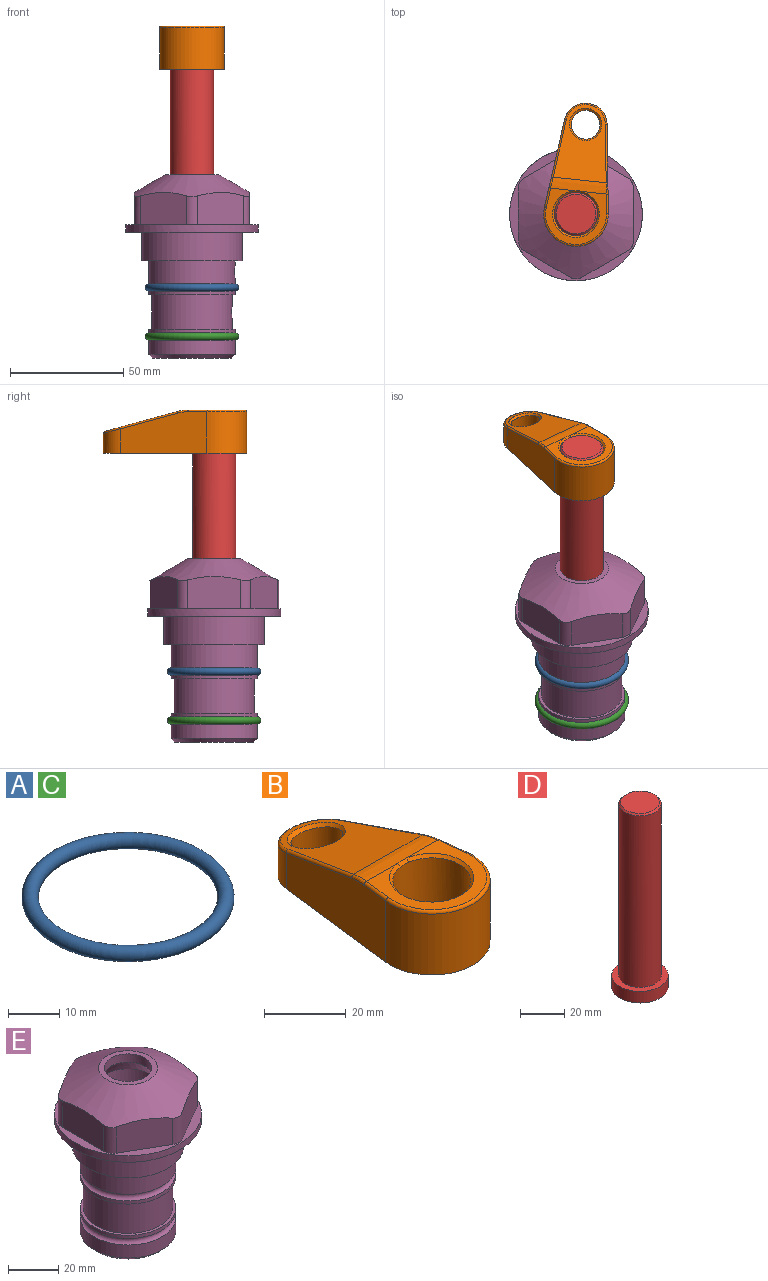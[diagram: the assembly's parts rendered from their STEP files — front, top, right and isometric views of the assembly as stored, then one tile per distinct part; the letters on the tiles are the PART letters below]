
ASSEMBLY  parts=5 mates=4
PART A: 1 faces, bbox 44.7x44.7x3.2 mm
  f0: torus R=19.05mm, axis (0,0,1), area 1193.9mm2
PART B: 31 faces, bbox 31.7x65.5x19.8 mm
  f0: plane 39.12x18.26mm, normal (0.99,0.12,0), area 612.2mm2, adj f1,f4,f7,f11,f13,f15
  f1: cylinder r=9.53mm len=18.91mm, axis (0,0,-1), area 296.1mm2, adj f0,f2,f7,f17
  f2: plane 39.12x18.26mm, normal (-0.99,0.12,0), area 612.2mm2, adj f1,f4,f7,f12,f14,f16
  f3: cylinder r=6.35mm len=12.7mm, axis (0,0,-1), area 362.4mm2, adj f7,f18
  f4: cylinder r=14.29mm len=28.58mm, axis (0,0,-1), area 882.2mm2, adj f0,f2,f7,f10
  f5: cylinder r=9.53mm len=19.05mm, axis (0,0,-1), area 1092.6mm2, adj f7,f19,f20
  f6: plane 26.99x23.69mm, normal (0,0,1), area 216.2mm2, adj f9,f10,f11,f12,f19
  f7: plane 63.5x28.58mm, normal (0,0,-1), area 661.8mm2, adj f0,f1,f2,f3,f4,f5,f22,f23
  f8: plane 33.52x23.6mm, normal (0,0.26,0.97), area 486mm2, adj f9,f15,f16,f17,f18
  f9: cylinder r=19.05mm len=24.72mm, axis (1,0,0), area 120.4mm2, adj f6,f8,f13,f14,f20
  f10: torus R=13.49mm, axis (0,0,1), area 59mm2, adj f4,f6,f11,f12
  f11: cylinder r=0.79mm len=8.67mm, axis (0.12,-0.99,0), area 10.8mm2, adj f0,f6,f10,f13
  f12: cylinder r=0.79mm len=8.67mm, axis (0.12,0.99,0), area 10.8mm2, adj f2,f6,f10,f14
  f13: bspline ~4.95x1.42mm, area 6.1mm2, adj f0,f9,f11,f15
  f14: bspline ~4.95x1.42mm, area 6.1mm2, adj f2,f9,f12,f16
  f15: cylinder r=0.79mm len=25.95mm, axis (0.12,-0.96,0.26), area 32.9mm2, adj f0,f8,f13,f17
  f16: cylinder r=0.79mm len=25.95mm, axis (0.12,0.96,-0.26), area 32.9mm2, adj f2,f8,f14,f17
  f17: bspline ~18.91x8.38mm, area 30mm2, adj f1,f8,f15,f16
  f18: bspline ~14.29x14.29mm, area 48.3mm2, adj f3,f8
  f19: cone r=9.53mm half-angle=45deg, axis (0,0,1), area 66.5mm2, adj f5,f6,f20
  f20: bspline ~3.22x0.96mm, area 3.5mm2, adj f5,f9,f19
  f21: plane 2.75x2.72mm, normal (0,0,-1), area 2.9mm2, adj f23,f25,f28
  f22: plane 23.05x15.88mm, normal (-0.99,-0.12,0), area 323.6mm2, adj f7,f25,f26,f27,f28,f29
  f23: plane 23.05x15.88mm, normal (0.99,-0.12,0), area 323.6mm2, adj f7,f21,f25,f27,f28,f30
  f24: cylinder r=9.53mm len=10.69mm, axis (0,0,-1), area 114.7mm2, adj f7,f27,f29,f30
  f25: cylinder r=12.7mm len=20.59mm, axis (0,0,-1), area 381.1mm2, adj f7,f21,f22,f23,f26,f28
  f26: plane 2.75x2.72mm, normal (0,0,-1), area 2.9mm2, adj f22,f25,f28
  f27: plane 19.72x18.37mm, normal (0,-0.26,-0.97), area 291.8mm2, adj f22,f23,f24,f28,f29,f30
  f28: cylinder r=15.88mm len=19.92mm, axis (1,0,0), area 54.8mm2, adj f21,f22,f23,f25,f26,f27
  f29: cylinder r=1.59mm len=11mm, axis (0,0,-1), area 34.7mm2, adj f7,f22,f24,f27
  f30: cylinder r=1.59mm len=11mm, axis (0,0,-1), area 34.7mm2, adj f7,f23,f24,f27
PART C: same geometry as A
PART D: 6 faces, bbox 25.4x25.4x101.6 mm
  f0: plane 17.46x17.46mm, normal (0,0,1), area 239.5mm2, adj f5
  f1: plane 25.4x25.4mm, normal (0,0,-1), area 506.7mm2, adj f2
  f2: cylinder r=12.7mm len=25.4mm, axis (0,0,1), area 506.7mm2, adj f1,f3
  f3: plane 25.4x25.4mm, normal (0,0,1), area 221.7mm2, adj f2,f4
  f4: cylinder r=9.53mm len=94.46mm, axis (0,0,1), area 5653mm2, adj f3,f5
  f5: cone r=8.73mm half-angle=45deg, axis (0,0,-1), area 64.4mm2, adj f0,f4
PART E: 36 faces, bbox 58.7x58.7x81 mm
  f0: cylinder r=17.78mm len=35.56mm, axis (0,0,1), area 1670.8mm2, adj f23,f24,f31
  f1: cylinder r=19.05mm len=38.1mm, axis (0,0,1), area 1191.9mm2, adj f26,f27,f30
  f2: plane 58.66x58.66mm, normal (0,0,-1), area 1150.6mm2, adj f3,f28
  f3: cylinder r=29.33mm len=58.66mm, axis (0,0,-1), area 585.1mm2, adj f2,f4
  f4: plane 58.66x58.66mm, normal (0,0,1), area 475.9mm2, adj f3,f5,f6,f7,f8,f9,f10,f11
  f5: plane 20.32x14.34mm, normal (-0.5,0.87,0), area 324.4mm2, adj f4,f15,f16,f17
  f6: plane 20.32x14.34mm, normal (0.5,0.87,0), area 324.4mm2, adj f4,f14,f15,f17
  f7: plane 23.48x14.34mm, normal (1,0,0), area 324.4mm2, adj f4,f13,f14,f17
  f8: plane 20.32x14.34mm, normal (0.5,-0.87,0), area 324.4mm2, adj f4,f12,f13,f17
  f9: plane 20.32x14.34mm, normal (-0.5,-0.87,0), area 324.4mm2, adj f4,f11,f12,f17
  f10: plane 23.48x14.34mm, normal (-1,0,0), area 324.4mm2, adj f4,f11,f16,f17
  f11: cylinder r=5.08mm len=12.85mm, axis (0,0,-1), area 67.2mm2, adj f4,f9,f10,f17
  f12: cylinder r=5.08mm len=12.85mm, axis (0,0,-1), area 67.2mm2, adj f4,f8,f9,f17
  f13: cylinder r=5.08mm len=12.85mm, axis (0,0,-1), area 67.2mm2, adj f4,f7,f8,f17
  f14: cylinder r=5.08mm len=12.85mm, axis (0,0,-1), area 67.2mm2, adj f4,f6,f7,f17
  f15: cylinder r=5.08mm len=12.85mm, axis (0,0,-1), area 67.2mm2, adj f4,f5,f6,f17
  f16: cylinder r=5.08mm len=12.85mm, axis (0,0,-1), area 67.2mm2, adj f4,f5,f10,f17
  f17: cone r=11.73mm half-angle=60deg, axis (0,0,-1), area 2071.8mm2, adj f5,f6,f7,f8,f9,f10,f11,f12
  f18: plane 23.46x23.46mm, normal (0,0,1), area 147.4mm2, adj f17,f35
  f19: plane 34.93x34.93mm, normal (0,0,-1), area 958mm2, adj f29
  f20: cylinder r=19.05mm len=38.1mm, axis (0,0,1), area 760.1mm2, adj f21,f29
  f21: torus R=19.05mm, axis (0,0,1), area 565.3mm2, adj f20,f22
  f22: cylinder r=19.05mm len=38.1mm, axis (0,0,1), area 190mm2, adj f21,f23
  f23: plane 38.1x38.1mm, normal (0,0,1), area 146.9mm2, adj f0,f22
  f24: plane 38.1x38.1mm, normal (0,0,-1), area 146.9mm2, adj f0,f25
  f25: cylinder r=19.05mm len=38.1mm, axis (0,0,1), area 190mm2, adj f24,f26
  f26: torus R=19.05mm, axis (0,0,1), area 565.3mm2, adj f1,f25
  f27: plane 44.45x44.45mm, normal (0,0,-1), area 411.7mm2, adj f1,f28
  f28: cylinder r=22.23mm len=44.45mm, axis (0,0,1), area 1773.5mm2, adj f2,f27
  f29: cone r=19.05mm half-angle=45deg, axis (0,0,1), area 257.5mm2, adj f19,f20
  f30: cylinder r=3.17mm len=6.75mm, axis (-1,0,0), area 128mm2, adj f1,f33
  f31: cylinder r=3.17mm len=6.35mm, axis (-1,0,0), area 102.5mm2, adj f0,f33
  f32: plane 25.4x25.4mm, normal (0,0,1), area 506.7mm2, adj f33
  f33: cylinder r=12.7mm len=66.42mm, axis (0,0,-1), area 5236.2mm2, adj f30,f31,f32,f34
  f34: cone r=9.53mm half-angle=30deg, axis (0,0,-1), area 443.4mm2, adj f33,f35
  f35: cylinder r=9.53mm len=19.05mm, axis (0,0,-1), area 240.9mm2, adj f18,f34
PLACE A at identity
PLACE B rot(axis=(0,0,-1),6.1deg) t=(0,0,27.55)mm
PLACE C t=(0,0,-21.59)mm
PLACE D rot(axis=(0,0,-1),6.1deg) t=(0,0,27.55)mm
PLACE E at identity fixed
MATE cylindrical E.f0 <-> D.f2  axis (0,0,1) through (0,0,-50.55)mm
MATE fastened E.f0 <-> A.f0  axis (0,0,1) through (0,0,-24.51)mm
MATE fastened B.f4 <-> D.f2  axis (0,0,1) through (0,0,91.05)mm
MATE fastened E.f0 <-> C.f0  axis (0,0,1) through (0,0,-46.1)mm
